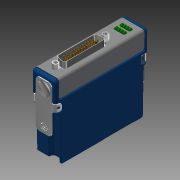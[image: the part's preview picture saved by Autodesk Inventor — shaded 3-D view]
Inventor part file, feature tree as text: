
AUTODESK INVENTOR PART (.ipt)
format: ipt  version: 2013 (Build 170138000, 138)  size: 8,074,752 bytes
history: native  units: mm
features: other x3, imported_body x1, sketch x1, fillet x1, extrude x1
ambient origin geometry x8: Origin, YZ Plane, XZ Plane, XY Plane, X Axis, Y Axis, Z Axis, Center Point
bodies: Solid1 (feature_tree)
feature tree (7):
  imported_body  "Base1"
  other  "RIGHT"
  other  "TOP"
  other  "FRONT"
  sketch  "Sketch2"  dims[d0=25.4mm d1=2.54mm d3=10.0mm d5=130.0mm d6=25.4mm d7=2.54mm d9=10.0mm d11=120.0mm d12=1.397mm d13=1.397mm d14=1.27mm d15=1.008245mm d17=0.0mm d18=25.4mm d19=0.381mm]
  fillet  "Fillet1"  [1 undecoded]
  extrude  "Extrusion1"  [1 undecoded]
note: 2 required parameter values undecoded (feature->parameter linkage not recoverable at this tier; creation-order binding heuristic only, values carry confidence <= 0.55)
